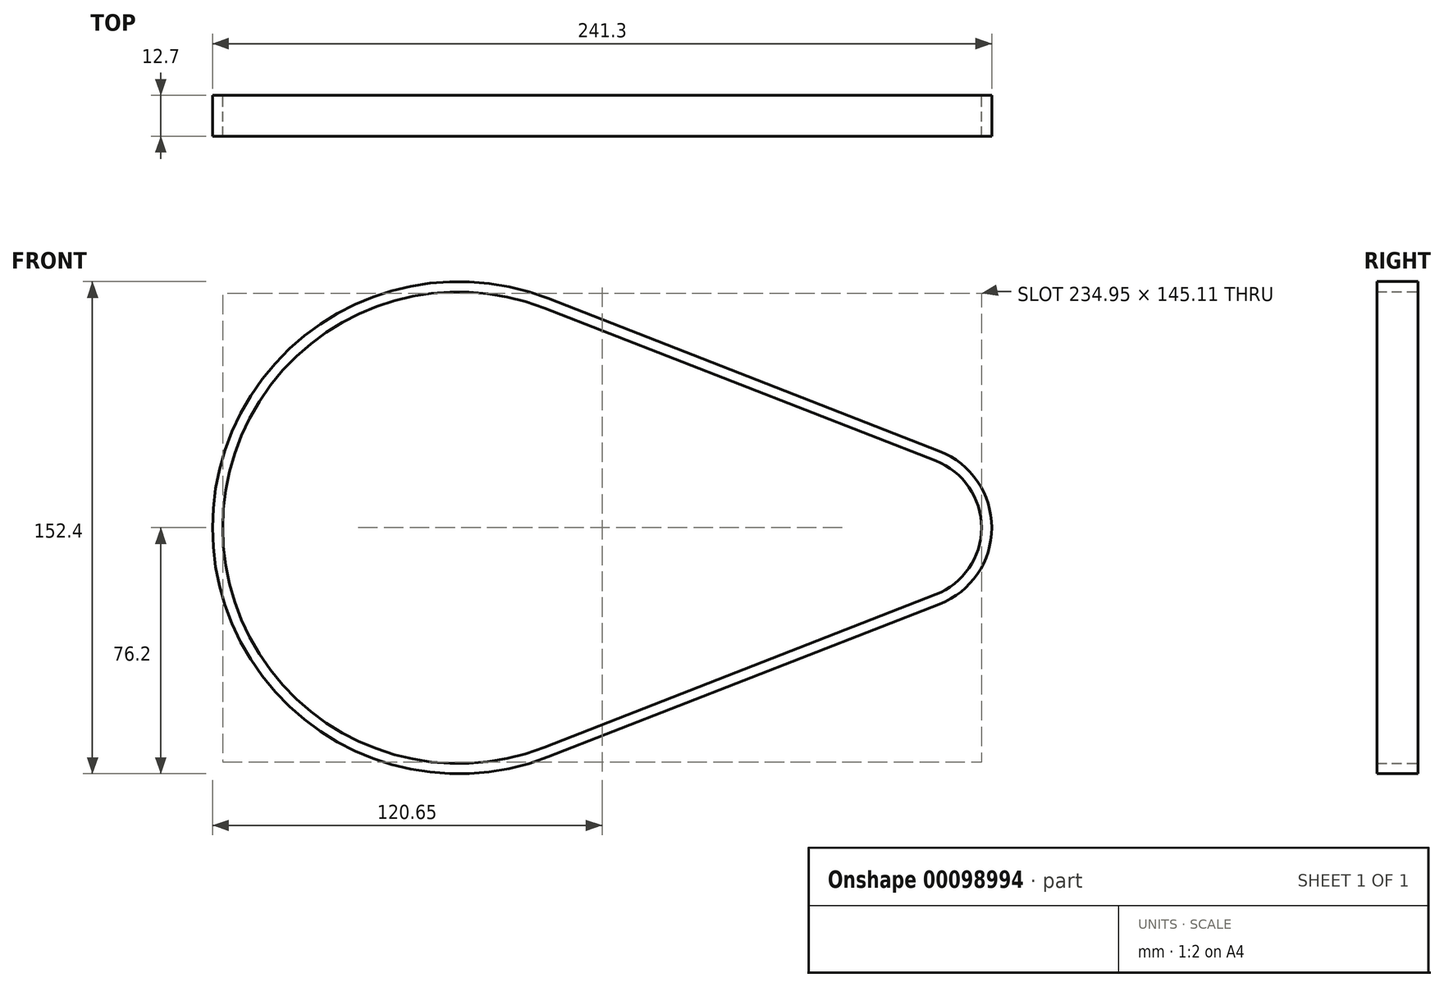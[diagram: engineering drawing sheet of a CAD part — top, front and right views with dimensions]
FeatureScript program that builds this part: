
annotation { "Feature Type Name" : "Feature", "Feature Type Description" : "" }
export const myFeature = defineFeature(function(context is Context, id is Id, definition is map)
    precondition{}
    {
        {
            var Q0;
            Q0=qCreatedBy(makeId("Front.planeOp"),FACE);
            var sketch = newSketch(context, id + "F0", { "sketchPlane" : qUnion([Q0])});
            skArc(sketch, "E0", {"start": v(26.55, 68.03) * mm, "mid": v(-73.02, 0) * mm, "end": v(26.55, -68.03) * mm});
            skArc(sketch, "E1", {"start": v(147.78, -20.7) * mm, "mid": v(161.93, 0) * mm, "end": v(147.78, 20.7) * mm});
            skLineSegment(sketch, "E2", {"start": v(26.55, 68.03) * mm, "end": v(147.78, 20.7) * mm});
            skLineSegment(sketch, "E3", {"start": v(26.55, -68.03) * mm, "end": v(147.78, -20.7) * mm});
            skArc(sketch, "E4.0", {"start": v(148.94, -23.66) * mm, "mid": v(165.1, 0) * mm, "end": v(148.94, 23.66) * mm});
            skLineSegment(sketch, "E4.1", {"start": v(27.7, -70.98) * mm, "end": v(148.94, -23.66) * mm});
            skArc(sketch, "E4.2", {"start": v(27.7, 70.98) * mm, "mid": v(-76.2, 0) * mm, "end": v(27.7, -70.98) * mm});
            skLineSegment(sketch, "E4.3", {"start": v(27.7, 70.98) * mm, "end": v(148.94, 23.66) * mm});
            skSolve(sketch);
        }
        {
            var Q0;
            Q0=makeQuery(id+"F0.imprint","IMPRINT",FACE,{"disambiguationData":[TD([[makeQuery(id+"F0.imprint","IMPRINT",EDGE,{"derivedFrom":sQuery(id+"F0.wireOp",EDGE,"E0")}),-1.0]])]});
            extrude(context, id + "F1", {"entities" : qUnion([Q0]), "depth" : 12.7 * mm});
        }
    });
